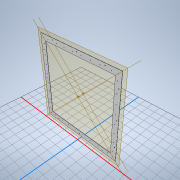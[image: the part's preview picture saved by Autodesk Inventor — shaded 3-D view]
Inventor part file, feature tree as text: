
AUTODESK INVENTOR PART (.ipt)
format: ipt  version: 2021 (Build 250183000, 183)  size: 224,768 bytes
history: native  units: mm
features: other x14, reference x10, extrude x3, sketch x3, pattern_linear x1, pattern_circular x1
ambient origin geometry x8: Origin, YZ Plane, XZ Plane, XY Plane, X Axis, Y Axis, Z Axis, Center Point
bodies: Body1 (feature_tree)
feature tree (32):
  other  "Bryła1"
  other  "Płaszczyzna konstrukcyjna1"
  extrude  "Wyciągnięcie proste1"  Depth=6.0mm
  extrude  "Wyciągnięcie proste2"  Depth=6.0mm
  pattern_linear  "Szyk prostokątny1"  Spacing1=6.0mm  [1 undecoded]
  other  "Oś konstrukcyjna5"
  pattern_circular  "Szyk kołowy1"  [2 undecoded]
  extrude  "Wyciągnięcie proste3"  Depth=60.0mm
  sketch  "Szkic1"
  reference  "Odniesienie1"
  reference  "Odniesienie2"
  reference  "Odniesienie3"
  reference  "Odniesienie4"
  reference  "Odniesienie5"
  reference  "Odniesienie6"
  reference  "Odniesienie7"
  reference  "Odniesienie8"
  sketch  "Szkic2"
  reference  "Odniesienie9"
  other  "Oś konstrukcyjna1"
  other  "Oś konstrukcyjna2"
  other  "Punkt konstrukcyjny1"
  other  "Oś konstrukcyjna3"
  other  "Oś konstrukcyjna4"
  other  "Punkt konstrukcyjny2"
  sketch  "Szkic3"
  reference  "Odniesienie10"
  parser-record x1  (decoder bookkeeping rows leaked as tree rows — omitted from the tree; the rows remain in map.json)
  other  "zespolokno.iam"
  other  "rama:1"
  other  "glas:1"
  other  "Zespół1"
note: 3 required parameter values undecoded (feature->parameter linkage not recoverable at this tier; creation-order binding heuristic only, values carry confidence <= 0.55)
note: 1 file-system path scrubbed to <path> (originals preserved in map.json)
